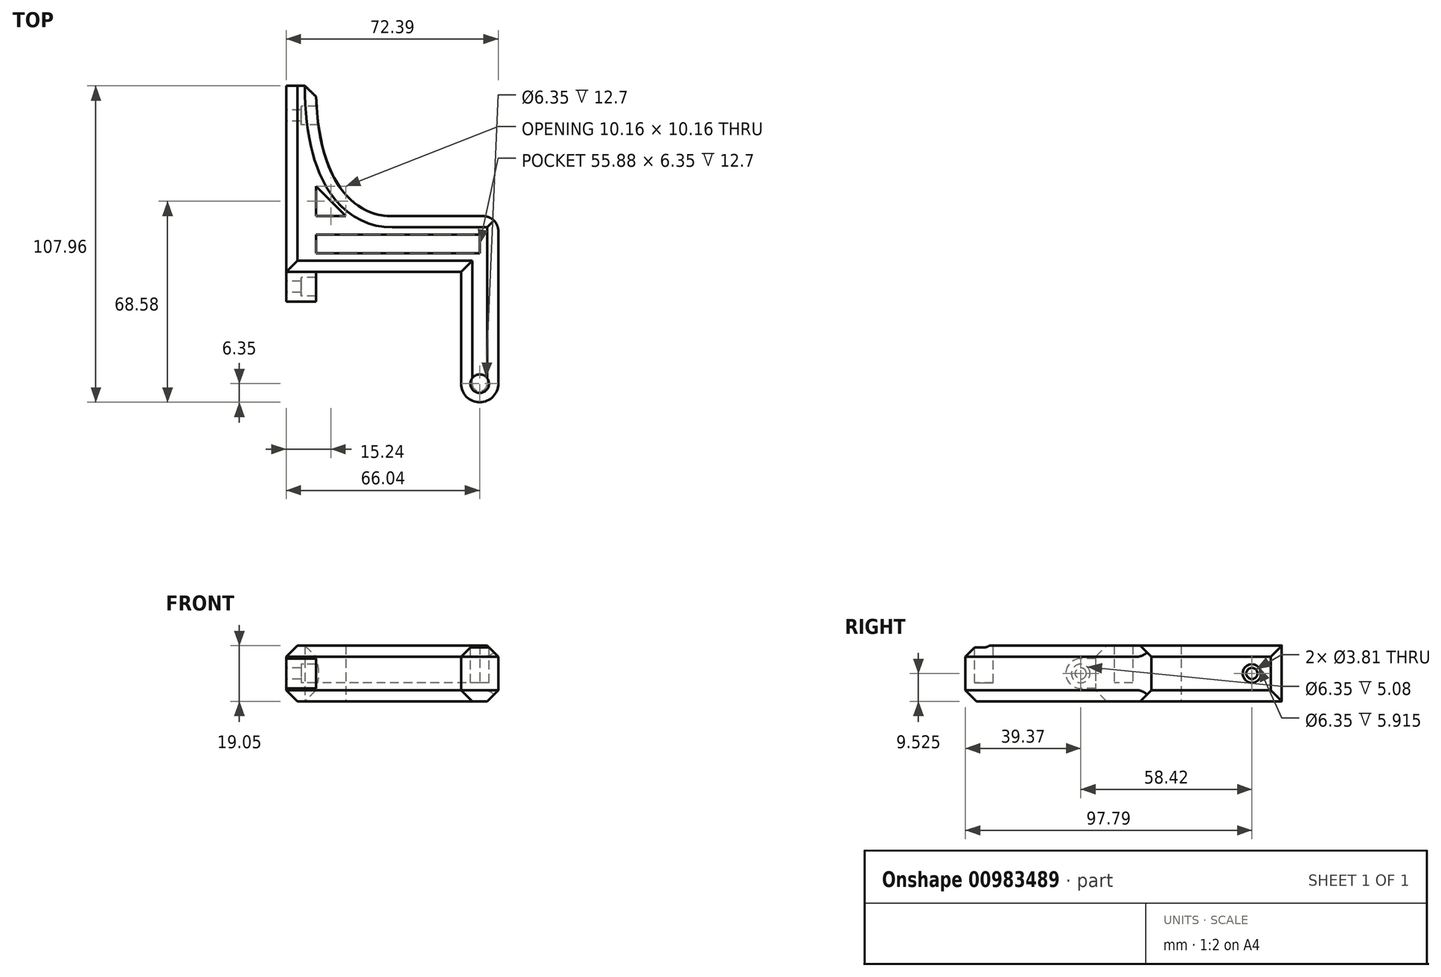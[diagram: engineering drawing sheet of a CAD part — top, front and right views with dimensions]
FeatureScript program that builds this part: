
annotation { "Feature Type Name" : "Feature", "Feature Type Description" : "" }
export const myFeature = defineFeature(function(context is Context, id is Id, definition is map)
    precondition{}
    {
        {
            var Q0;
            Q0=qCreatedBy(makeId("Top.planeOp"),FACE);
            var sketch = newSketch(context, id + "F0", { "sketchPlane" : qUnion([Q0])});
            skLineSegment(sketch, "E0", {"start": v(0, 0) * mm, "end": v(0, 63.5) * mm});
            skLineSegment(sketch, "E1", {"start": v(0, 63.5) * mm, "end": v(10.16, 63.5) * mm});
            skLineSegment(sketch, "E2", {"start": v(0, 0) * mm, "end": v(72.39, 0) * mm});
            skLineSegment(sketch, "E3", {"start": v(72.4, 0) * mm, "end": v(72.4, 19.05) * mm});
            skLineSegment(sketch, "E4", {"start": v(72.4, 19.05) * mm, "end": v(36.2, 19.05) * mm});
            skLineSegment(sketch, "E5", {"start": v(10.16, 19.05) * mm, "end": v(10.16, 29.21) * mm});
            skLineSegment(sketch, "E6", {"start": v(10.16, 29.21) * mm, "end": v(20.32, 19.05) * mm});
            skLineSegment(sketch, "E7", {"start": v(20.32, 19.05) * mm, "end": v(10.16, 19.05) * mm});
            skLineSegment(sketch, "E8", {"start": v(36.2, 63.55) * mm, "end": v(36.2, 0) * mm, "construction": true});
            skPoint(sketch, "E9.positionSnap0", {"position": v(72.4, 9.53) * mm});
            skLineSegment(sketch, "E10.bottom", {"start": v(66.04, 12.7) * mm, "end": v(10.16, 12.7) * mm});
            skLineSegment(sketch, "E10.top", {"start": v(66.04, 6.35) * mm, "end": v(10.16, 6.35) * mm});
            skLineSegment(sketch, "E10.left", {"start": v(66.04, 12.7) * mm, "end": v(66.04, 6.35) * mm});
            skLineSegment(sketch, "E10.right", {"start": v(10.16, 12.7) * mm, "end": v(10.16, 6.35) * mm});
            skPoint(sketch, "E10.middle", {"position": v(36.2, 9.53) * mm});
            skFitSpline(sketch, "E11", {"points": [v(10.16, 63.5) * mm, v(36.2, 19.05) * mm], "startDerivative": vector(0, -95.25) * mm, "endDerivative": vector(41.3, 0) * mm});
            skPoint(sketch, "E12", {"position": v(0, 31.75) * mm});
            skLineSegment(sketch, "E13", {"start": v(72.4, 0) * mm, "end": v(72.4, -38.1) * mm});
            skLineSegment(sketch, "E14", {"start": v(59.7, 0) * mm, "end": v(59.7, -38.1) * mm});
            skArc(sketch, "E15", {"start": v(59.69, -38.1) * mm, "mid": v(66.04, -44.45) * mm, "end": v(72.4, -38.1) * mm});
            skSolve(sketch);
        }
        {
            var Q0;
            {var subQ1=sQuery(id+"F0.wireOp",EDGE,"E0");Q0=makeQuery(id+"F0.imprint","IMPRINT",FACE,{"disambiguationData":[TD([[makeQuery(id+"F0.imprint","IMPRINT",EDGE,{"derivedFrom":subQ1}),-1.0]])]});}
            var Q1;
            {var subQ0=sQuery(id+"F0.wireOp",EDGE,"E13");Q1=makeQuery(id+"F0.imprint","IMPRINT",FACE,{"disambiguationData":[TD([[makeQuery(id+"F0.imprint","IMPRINT",EDGE,{"derivedFrom":subQ0}),-1.0]])]});}
            extrude(context, id + "F1", {"entities" : qUnion([Q0, Q1]), "depth" : 19.05 * mm, "offsetDistance" : 25.4 * mm});
        }
        {
            var Q0;
            Q0=makeQuery(id+"F0.imprint","IMPRINT",FACE,{"disambiguationData":[TD([[makeQuery(id+"F0.imprint","IMPRINT",EDGE,{"derivedFrom":sQuery(id+"F0.wireOp",EDGE,"E10.bottom")}),1.0]])]});
            extrude(context, id + "F2", {"entities" : qUnion([Q0]), "operationType" : NewBodyOperationType.ADD, "depth" : 6.35 * mm, "offsetDistance" : 25.4 * mm});
        }
        {
            var Q0;
            Q0=makeQuery(id+"F1.opExtrude","CAP_FACE",FACE,{"disambiguationData":[OSD([sQuery(id+"F0.wireOp",EDGE,"E0"),sQuery(id+"F0.wireOp",EDGE,"E1"),sQuery(id+"F0.wireOp",EDGE,"E2"),sQuery(id+"F0.wireOp",EDGE,"E3"),sQuery(id+"F0.wireOp",EDGE,"E4"),sQuery(id+"F0.wireOp",EDGE,"E5"),sQuery(id+"F0.wireOp",EDGE,"E6"),sQuery(id+"F0.wireOp",EDGE,"E7"),sQuery(id+"F0.wireOp",EDGE,"E10.bottom"),sQuery(id+"F0.wireOp",EDGE,"E10.top"),sQuery(id+"F0.wireOp",EDGE,"E10.left"),sQuery(id+"F0.wireOp",EDGE,"E10.right"),sQuery(id+"F0.wireOp",EDGE,"E11"),sQuery(id+"F0.wireOp",EDGE,"E13"),sQuery(id+"F0.wireOp",EDGE,"E14"),sQuery(id+"F0.wireOp",EDGE,"E15")])],"isStart":false});
            var sketch = newSketch(context, id + "F3", { "sketchPlane" : qUnion([Q0])});
            skCircle(sketch, "E16", {"center": v(66.04, -38.1) * mm, "radius": 3.18 * mm});
            skSolve(sketch);
        }
        {
            var Q0;
            Q0=makeQuery(id+"F3.imprint","IMPRINT",FACE,{"disambiguationData":[TD([[makeQuery(id+"F3.imprint","IMPRINT",EDGE,{"derivedFrom":sQuery(id+"F3.wireOp",EDGE,"E16")}),1.0]])]});
            extrude(context, id + "F4", {"entities" : qUnion([Q0]), "operationType" : NewBodyOperationType.REMOVE, "oppositeDirection" : true, "depth" : 12.7 * mm, "offsetDistance" : 25.4 * mm});
        }
        {
            var Q0;
            Q0=makeQuery(id+"F1.opExtrude","SWEPT_FACE",FACE,{"disambiguationData":[OSD([sQuery(id+"F0.wireOp",EDGE,"E0")])]});
            var sketch = newSketch(context, id + "F5", { "sketchPlane" : qUnion([Q0])});
            skLineSegment(sketch, "E17", {"start": v(-3.18, 9.53) * mm, "end": v(0, 9.53) * mm, "construction": true});
            skLineSegment(sketch, "E18", {"start": v(0, 14.6) * mm, "end": v(5.08, 14.6) * mm});
            skLineSegment(sketch, "E19.MirrorCS", {"start": v(0, 4.45) * mm, "end": v(5.08, 4.45) * mm});
            skArc(sketch, "E20", {"start": v(5.08, 4.45) * mm, "mid": v(10.16, 9.53) * mm, "end": v(5.08, 14.6) * mm});
            skCircle(sketch, "E21", {"center": v(5.08, 9.53) * mm, "radius": 3.18 * mm});
            skCircle(sketch, "E22", {"center": v(-53.34, 9.53) * mm, "radius": 3.18 * mm});
            skPoint(sketch, "E22.centerSnap0", {"position": v(-63.5, 9.53) * mm});
            skCircle(sketch, "E23", {"center": v(-53.34, 9.53) * mm, "radius": 1.9 * mm});
            skCircle(sketch, "E24", {"center": v(5.08, 9.53) * mm, "radius": 1.9 * mm});
            skSolve(sketch);
        }
        {
            var Q0;
            {var subQ1=sQuery(id+"F5.wireOp",EDGE,"E18");Q0=makeQuery(id+"F5.imprint","IMPRINT",FACE,{"disambiguationData":[TD([[makeQuery(id+"F5.imprint","IMPRINT",EDGE,{"derivedFrom":subQ1}),-1.0]])]});}
            extrude(context, id + "F6", {"entities" : qUnion([Q0]), "operationType" : NewBodyOperationType.ADD, "oppositeDirection" : true, "depth" : 10.16 * mm, "offsetDistance" : 25.4 * mm});
        }
        {
            var Q0;
            Q0=makeQuery(id+"F5.imprint","IMPRINT",FACE,{"disambiguationData":[TD([[makeQuery(id+"F5.imprint","IMPRINT",EDGE,{"derivedFrom":sQuery(id+"F5.wireOp",EDGE,"E21")}),1.0]])]});
            extrude(context, id + "F7", {"entities" : qUnion([Q0]), "operationType" : NewBodyOperationType.ADD, "oppositeDirection" : true, "depth" : 5.08 * mm, "offsetDistance" : 25.4 * mm});
        }
        {
            var Q0;
            Q0=makeQuery(id+"F5.imprint","IMPRINT",FACE,{"disambiguationData":[TD([[makeQuery(id+"F5.imprint","IMPRINT",EDGE,{"derivedFrom":sQuery(id+"F5.wireOp",EDGE,"E23")}),1.0]])]});
            extrude(context, id + "F8", {"entities" : qUnion([Q0]), "operationType" : NewBodyOperationType.REMOVE, "endBound" : BoundingType.THROUGH_ALL, "oppositeDirection" : true, "depth" : 25.4 * mm, "offsetDistance" : 25.4 * mm});
        }
        {
            var Q0;
            Q0=makeQuery(id+"F5.imprint","IMPRINT",FACE,{"disambiguationData":[TD([[makeQuery(id+"F5.imprint","IMPRINT",EDGE,{"derivedFrom":sQuery(id+"F5.wireOp",EDGE,"E22")}),1.0]])]});
            extrude(context, id + "F9", {"entities" : qUnion([Q0]), "operationType" : NewBodyOperationType.REMOVE, "endBound" : BoundingType.THROUGH_ALL, "oppositeDirection" : true, "depth" : 25.4 * mm, "offsetDistance" : 25.4 * mm, "hasSecondDirection" : true, "secondDirectionOppositeDirection" : true, "secondDirectionDepth" : 5.08 * mm});
        }
        {
            var Q0;
            Q0=makeQuery(id+"F1.opExtrude","CAP_EDGE",EDGE,{"disambiguationData":[OSD([sQuery(id+"F0.wireOp",EDGE,"E3"),sQuery(id+"F0.wireOp",EDGE,"E13")])],"isStart":false});
            var Q1;
            Q1=makeQuery(id+"F1.opExtrude","CAP_EDGE",EDGE,{"disambiguationData":[OSD([sQuery(id+"F0.wireOp",EDGE,"E2")])],"isStart":false});
            var Q2;
            Q2=makeQuery(id+"F1.opExtrude","CAP_EDGE",EDGE,{"disambiguationData":[OSD([sQuery(id+"F0.wireOp",EDGE,"E0")])],"isStart":false});
            var Q3;
            Q3=makeQuery(id+"F1.opExtrude","CAP_EDGE",EDGE,{"disambiguationData":[OSD([sQuery(id+"F0.wireOp",EDGE,"E4")])],"isStart":false});
            var Q4;
            Q4=makeQuery(id+"F1.opExtrude","SWEPT_EDGE",EDGE,{"disambiguationData":[OSD([sQuery(id+"F0.wireOp",EDGE,"E1"),sQuery(id+"F0.wireOp",EDGE,"E11")])]});
            var Q5;
            Q5=makeQuery(id+"F1.opExtrude","CAP_EDGE",EDGE,{"disambiguationData":[OSD([sQuery(id+"F0.wireOp",EDGE,"E2")])],"isStart":true});
            var Q6;
            Q6=makeQuery(id+"F1.opExtrude","CAP_EDGE",EDGE,{"disambiguationData":[OSD([sQuery(id+"F0.wireOp",EDGE,"E14")])],"isStart":true});
            var Q7;
            Q7=makeQuery(id+"F1.opExtrude","CAP_EDGE",EDGE,{"disambiguationData":[OSD([sQuery(id+"F0.wireOp",EDGE,"E4")])],"isStart":true});
            var Q8;
            Q8=makeQuery(id+"F1.opExtrude","CAP_EDGE",EDGE,{"disambiguationData":[OSD([sQuery(id+"F0.wireOp",EDGE,"E0")])],"isStart":true});
            chamfer(context, id + "F10", {"entities" : qUnion([Q0, Q1, Q2, Q3, Q4, Q5, Q6, Q7, Q8]), "chamferType" : ChamferType.OFFSET_ANGLE, "width" : 3.8 * mm, "oppositeDirection" : false, "angle" : 45 * degree, "tangentPropagation" : true});
        }
        {
            var Q0;
            Q0=makeQuery(id+"F1.opExtrude","SWEPT_EDGE",EDGE,{"disambiguationData":[OSD([sQuery(id+"F0.wireOp",EDGE,"E3"),sQuery(id+"F0.wireOp",EDGE,"E4")])]});
            fillet(context, id + "F11", {"entities" : qUnion([Q0]), "radius" : 5.08 * mm, "tangentPropagation" : true, "allowEdgeOverflow" : false});
        }
    });
